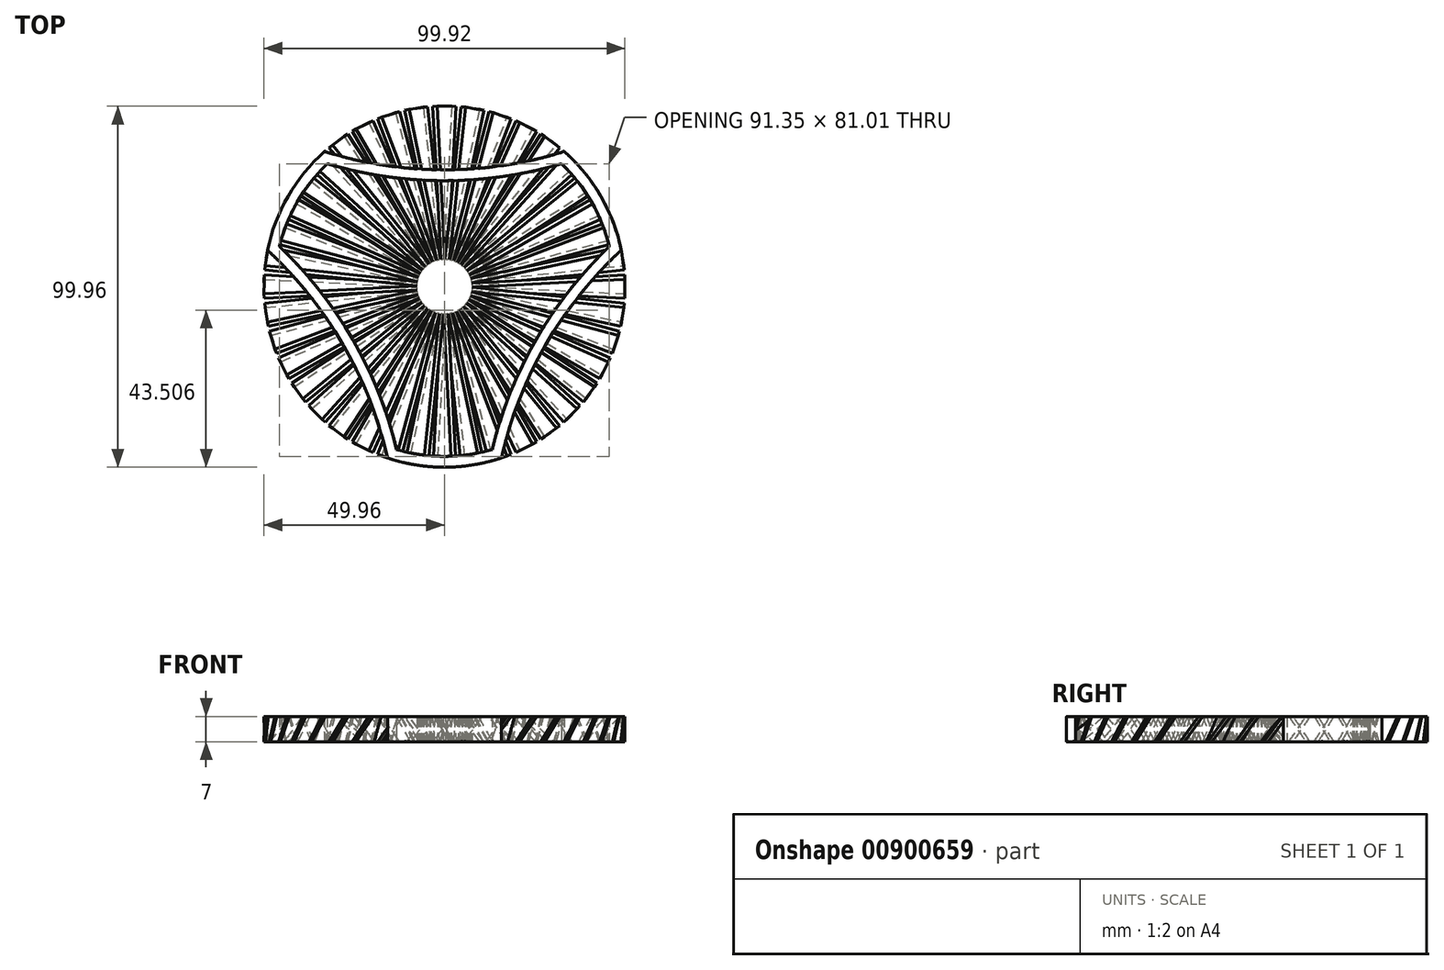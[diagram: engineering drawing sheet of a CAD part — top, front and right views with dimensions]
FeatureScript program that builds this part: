
annotation { "Feature Type Name" : "Feature", "Feature Type Description" : "" }
export const myFeature = defineFeature(function(context is Context, id is Id, definition is map)
    precondition{}
    {
        {
            var Q0;
            Q0=qCreatedBy(makeId("Top.planeOp"),FACE);
            var sketch = newSketch(context, id + "F0", { "sketchPlane" : qUnion([Q0])});
            skLineSegment(sketch, "E0.bottom", {"start": v(2.02, 49.96) * mm, "end": v(3.22, 49.9) * mm});
            skLineSegment(sketch, "E0.top", {"start": v(-3.22, -49.9) * mm, "end": v(-2.02, -49.96) * mm});
            skLineSegment(sketch, "E0.left", {"start": v(2.02, 49.96) * mm, "end": v(-3.22, -49.9) * mm});
            skLineSegment(sketch, "E0.right", {"start": v(3.22, 49.9) * mm, "end": v(-2.02, -49.96) * mm});
            skPoint(sketch, "E0.middle", {"position": v(0, 0) * mm});
            skSolve(sketch);
        }
        {
            var Q0;
            Q0=qCreatedBy(makeId("Top.planeOp"),FACE);
            cPlane(context, id + "F1", {"entities" : qUnion([Q0]), "cplaneType" : CPlaneType.OFFSET, "offset" : 7 * mm, "width" : 150 * mm, "height" : 150 * mm});
        }
        {
            var Q0;
            Q0=qCreatedBy(id+"F1.planeOp",FACE);
            var sketch = newSketch(context, id + "F2", { "sketchPlane" : qUnion([Q0])});
            skLineSegment(sketch, "E1.bottom", {"start": v(-3.22, 49.9) * mm, "end": v(-2.02, 49.96) * mm});
            skLineSegment(sketch, "E1.top", {"start": v(2.02, -49.96) * mm, "end": v(3.22, -49.9) * mm});
            skLineSegment(sketch, "E1.left", {"start": v(-3.22, 49.9) * mm, "end": v(2.02, -49.96) * mm});
            skLineSegment(sketch, "E1.right", {"start": v(-2.02, 49.96) * mm, "end": v(3.22, -49.9) * mm});
            skPoint(sketch, "E1.middle", {"position": v(0, 0) * mm});
            skSolve(sketch);
        }
        {
            var Q0;
            Q0=makeQuery(id+"F0.imprint","IMPRINT",FACE,{"disambiguationData":[TD([[makeQuery(id+"F0.imprint","IMPRINT",EDGE,{"derivedFrom":sQuery(id+"F0.wireOp",EDGE,"E0.bottom")}),-1.0]])]});
            var Q1;
            Q1=makeQuery(id+"F2.imprint","IMPRINT",FACE,{"disambiguationData":[TD([[makeQuery(id+"F2.imprint","IMPRINT",EDGE,{"derivedFrom":sQuery(id+"F2.wireOp",EDGE,"E1.bottom")}),-1.0]])]});
            loft(context, id + "F3", {"sheetProfilesArray" : [{ "sheetProfileEntities" : qUnion([Q0]) }, { "sheetProfileEntities" : qUnion([Q1]) }]});
        }
        {
            var Q0;
            Q0=qCreatedBy(makeId("Right.planeOp"),FACE);
            var sketch = newSketch(context, id + "F4", { "sketchPlane" : qUnion([Q0])});
            skLineSegment(sketch, "E2", {"start": v(0, -7.54) * mm, "end": v(0, 20.3) * mm});
            skSolve(sketch);
        }
        {
            var Q0;
            Q0=makeQuery(id+"F3.opLoft","SWEPT_BODY",BODY,{"disambiguationData":[OSD([makeQuery(id+"F0.imprint","IMPRINT",FACE,{"disambiguationData":[TD([[makeQuery(id+"F0.imprint","IMPRINT",EDGE,{"derivedFrom":sQuery(id+"F0.wireOp",EDGE,"E0.bottom")}),-1.0]])]}),makeQuery(id+"F2.imprint","IMPRINT",FACE,{"disambiguationData":[TD([[makeQuery(id+"F2.imprint","IMPRINT",EDGE,{"derivedFrom":sQuery(id+"F2.wireOp",EDGE,"E1.bottom")}),-1.0]])]})])]});
            var Q1;
            Q1=sQuery(id+"F4.wireOp",EDGE,"E2");
            circularPattern(context, id + "F5", {"entities" : qUnion([Q0]), "axis" : qUnion([Q1]), "angle" : 360 * degree, "instanceCount" : 40, "equalSpace" : true});
        }
        {
            var Q0;
            Q0=qCreatedBy(makeId("Top.planeOp"),FACE);
            var sketch = newSketch(context, id + "F6", { "sketchPlane" : qUnion([Q0])});
            skArc(sketch, "E3", {"start": v(-33.2, 37.38) * mm, "mid": v(-43.3, 25) * mm, "end": v(-48.98, 10.07) * mm});
            skLineSegment(sketch, "E4", {"start": v(-33.2, 37.38) * mm, "end": v(33.2, 37.38) * mm, "construction": true});
            skArc(sketch, "E5", {"start": v(-33.2, 37.38) * mm, "mid": v(0, 32.33) * mm, "end": v(33.2, 37.38) * mm});
            skArc(sketch, "E6.1.0", {"start": v(-15.77, -47.45) * mm, "mid": v(-28, -16.17) * mm, "end": v(-48.98, 10.07) * mm});
            skArc(sketch, "E6.2.0", {"start": v(48.98, 10.07) * mm, "mid": v(28, -16.17) * mm, "end": v(15.77, -47.45) * mm});
            skArc(sketch, "E7.trimOffspring", {"start": v(-15.77, -47.45) * mm, "mid": v(0, -50) * mm, "end": v(15.77, -47.45) * mm});
            skArc(sketch, "E8.trimOffspring", {"start": v(48.98, 10.07) * mm, "mid": v(43.3, 25) * mm, "end": v(33.2, 37.38) * mm});
            skArc(sketch, "E9.0", {"start": v(-32.44, 34.01) * mm, "mid": v(-40.7, 23.5) * mm, "end": v(-45.67, 11.09) * mm});
            skArc(sketch, "E9.1", {"start": v(45.67, 11.09) * mm, "mid": v(40.7, 23.5) * mm, "end": v(32.44, 34.01) * mm});
            skArc(sketch, "E9.2", {"start": v(45.67, 11.09) * mm, "mid": v(25.4, -14.67) * mm, "end": v(13.24, -45.1) * mm});
            skArc(sketch, "E9.3", {"start": v(-32.44, 34.01) * mm, "mid": v(0, 29.33) * mm, "end": v(32.44, 34.01) * mm});
            skArc(sketch, "E9.4", {"start": v(-13.24, -45.1) * mm, "mid": v(0, -47) * mm, "end": v(13.24, -45.1) * mm});
            skArc(sketch, "E9.5", {"start": v(-13.24, -45.1) * mm, "mid": v(-25.4, -14.67) * mm, "end": v(-45.67, 11.09) * mm});
            skCircle(sketch, "E10", {"center": v(0, 0) * mm, "radius": 11.2 * mm});
            skCircle(sketch, "E11", {"center": v(0, 0) * mm, "radius": 13.2 * mm});
            skSolve(sketch);
        }
        {
            var Q0;
            Q0 = qSketchRegion(id + "F6", true);
            extrude(context, id + "F7", {"entities" : qUnion([Q0]), "operationType" : NewBodyOperationType.ADD, "depth" : 7 * mm, "offsetDistance" : 25 * mm});
        }
        {
            var Q0;
            Q0=makeQuery(id+"F6.imprint","IMPRINT",FACE,{"disambiguationData":[TD([[makeQuery(id+"F6.imprint","IMPRINT",EDGE,{"derivedFrom":sQuery(id+"F6.wireOp",EDGE,"E3")}),1.0]])]});
            extrude(context, id + "F8", {"entities" : qUnion([Q0]), "depth" : 7 * mm, "offsetDistance" : 25 * mm});
        }
    });
